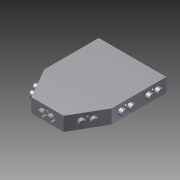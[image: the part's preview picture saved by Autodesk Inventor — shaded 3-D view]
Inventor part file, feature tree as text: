
AUTODESK INVENTOR PART (.ipt)
format: ipt  version: 2012 (Build 160160000, 160)  size: 265,216 bytes
history: native  units: mm
features: extrude x13, sketch x8
ambient origin geometry x8: Origin, YZ Plane, XZ Plane, XY Plane, X Axis, Y Axis, Z Axis, Center Point
bodies: Solid1 (feature_tree)
feature tree (21):
  extrude  "Extrusion1"  TaperAngle=150.0deg  [1 undecoded]
  sketch  "Sketch2"  dims[d6=91.026319mm d7=91.026319mm]
  extrude  "Extrusion2"  Depth=91.026319mm
  extrude  "Extrusion3"  Depth=140.933826mm
  sketch  "Sketch3"  dims[d8=83.483681mm d9=140.933826mm]
  extrude  "Extrusion4"  Depth=36.0mm TaperAngle=0.0deg
  extrude  "Extrusion5"  Depth=10.0mm TaperAngle=0.0deg
  sketch  "Sketch4"  dims[d10=140.933826mm d11=36.0mm d12=0.0mm]
  extrude  "Extrusion6"  Depth=3.0mm TaperAngle=0.0deg
  extrude  "Extrusion7"  Depth=10.0mm TaperAngle=0.0deg
  sketch  "Sketch5"  dims[d13=16.5mm d14=16.5mm d15=5.9mm d16=3.0mm d17=7.8mm d18=7.8mm d19=23.4mm d20=7.675mm d21=7.675mm d22=7.675mm d23=7.675mm d24=7.8mm d25=7.8mm d27=6.9mm d29=10.0mm d30=0.0mm]
  extrude  "Extrusion8"  Depth=3.0mm TaperAngle=0.0deg
  extrude  "Extrusion9"  Depth=70.466913mm
  sketch  "Sketch6"  dims[d31=3.0mm d32=0.0mm]
  extrude  "Extrusion10"  Depth=35.2335mm
  extrude  "Extrusion11"  Depth=3.0mm TaperAngle=0.0deg
  sketch  "Sketch7"  dims[d49=16.5mm d50=16.5mm d51=5.9mm d52=3.0mm d53=7.675mm d54=7.675mm d55=23.4mm d56=7.8mm d57=7.8mm d58=7.8mm d59=7.8mm d60=7.675mm d61=7.675mm d62=11.7mm d63=3.0mm d64=0.0mm]
  sketch  "Sketch8"  dims[d65=10.0mm d66=0.0mm d67=16.5mm d68=16.5mm d69=5.9mm d70=3.0mm d71=-7.675mm d72=7.675mm d73=23.4mm d74=7.8mm d75=7.8mm d76=7.8mm d77=7.8mm d78=7.675mm d79=7.675mm d80=6.9mm d81=11.7mm d82=6.9mm d83=10.0mm d84=0.0mm d85=3.0mm d86=0.0mm d87=16.5mm d88=16.5mm d89=5.9mm d90=3.0mm d91=7.675mm d92=7.675mm d93=23.4mm d94=7.8mm d95=7.8mm d96=7.8mm d97=7.8mm d98=7.675mm d99=7.675mm d100=6.9mm d101=11.7mm d102=6.9mm d103=70.466913mm d104=35.2335mm d105=3.0mm d106=0.0mm d107=10.0mm d108=0.0mm d125=87.255mm d126=43.6275mm d127=16.5mm d128=16.5mm d129=5.9mm d130=3.0mm d131=-7.8mm d132=7.8mm d133=23.4mm d134=7.675mm d135=7.675mm d136=7.675mm d137=7.675mm d138=7.8mm d139=7.8mm d140=11.7mm d141=6.9mm d142=11.7mm d143=10.0mm d144=0.0mm d145=3.0mm d146=0.0mm d147=16.5mm d148=16.5mm d149=5.9mm d150=3.0mm d151=-7.675mm d152=7.675mm d153=23.4mm d154=7.8mm d155=7.8mm d156=7.8mm d157=7.8mm d158=7.675mm d159=7.675mm d160=6.9mm d161=11.7mm d162=6.9mm d165=3.0mm d166=0.0mm d167=10.0mm d168=0.0mm]
  extrude  "Extrusion12"  Depth=10.0mm TaperAngle=0.0deg
  extrude  "Extrusion13"  Depth=87.255mm
  sketch  "Sketch1"  dims[d0=120.0deg d1=219.764931mm d2=174.51mm d3=120.0deg d4=150.0deg d5=150.0deg]
note: 1 required parameter value undecoded (feature->parameter linkage not recoverable at this tier; creation-order binding heuristic only, values carry confidence <= 0.55)
